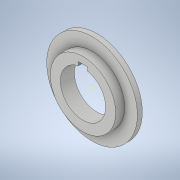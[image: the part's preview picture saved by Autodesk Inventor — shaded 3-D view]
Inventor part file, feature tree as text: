
AUTODESK INVENTOR PART (.ipt)
format: ipt  version: 2021 (Build 250183000, 183)  size: 126,464 bytes
history: native  units: in
note: dims shown in document units (in); Inventor stores cm internally (conversion verified against a paired STEP export)
features: sketch x3, revolve x1, extrude x1
ambient origin geometry x8: Origin, YZ Plane, XZ Plane, XY Plane, X Axis, Y Axis, Z Axis, Center Point
bodies: Solid1 (feature_tree)
feature tree (5):
  revolve  "Revolution1"  [1 undecoded]
  extrude  "Extrusion1"  Depth=0.137in
  sketch  "Sketch3"  dims[d4=90.0deg d5=1.25in d6=0.25in d7=0.1in d8=0.0in d9=0.0in]
  sketch  "Sketch1"  dims[d0=0.9in d1=0.25in]
  sketch  "Sketch2"  dims[d2=0.35in d3=0.137in]
note: 1 required parameter value undecoded (feature->parameter linkage not recoverable at this tier; creation-order binding heuristic only, values carry confidence <= 0.55)
